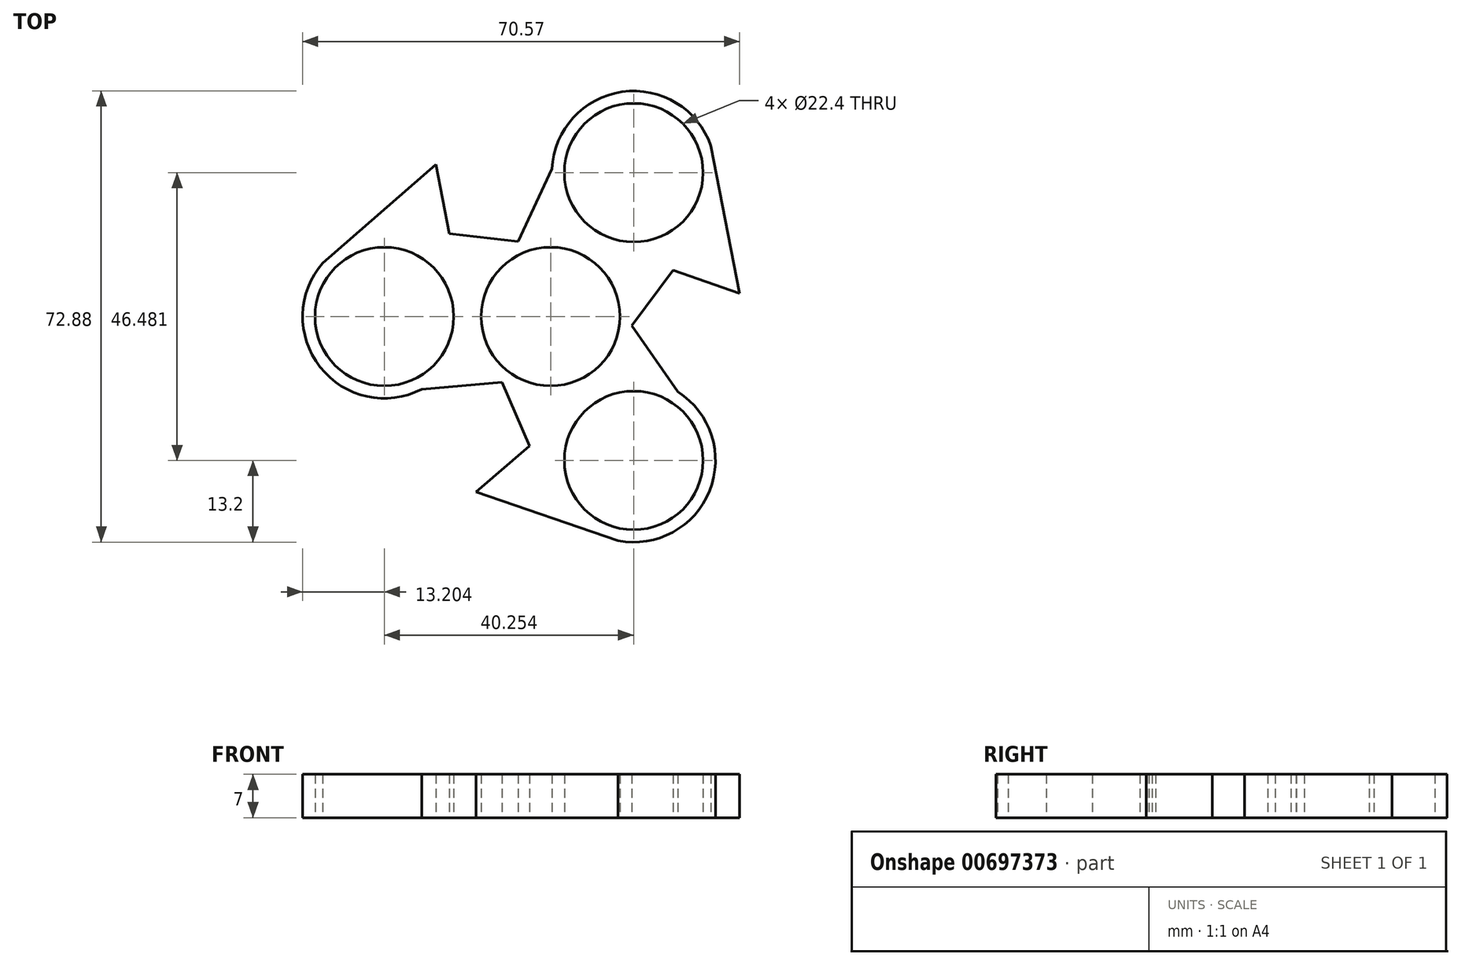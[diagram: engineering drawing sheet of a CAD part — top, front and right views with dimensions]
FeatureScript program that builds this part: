
annotation { "Feature Type Name" : "Feature", "Feature Type Description" : "" }
export const myFeature = defineFeature(function(context is Context, id is Id, definition is map)
    precondition{}
    {
        {
            var Q0;
            Q0=qCreatedBy(makeId("Top.planeOp"),FACE);
            var sketch = newSketch(context, id + "F0", { "sketchPlane" : qUnion([Q0])});
            skCircle(sketch, "E0", {"center": v(0, 0) * mm, "radius": 11.2 * mm});
            skCircle(sketch, "E1", {"center": v(-26.84, 0) * mm, "radius": 11.2 * mm});
            skArc(sketch, "E2", {"start": v(-34.03, 11.07) * mm, "mid": v(-38.25, -6.63) * mm, "end": v(-20.79, -11.73) * mm});
            skCircle(sketch, "E3.1.0", {"center": v(13.42, -23.24) * mm, "radius": 11.2 * mm});
            skArc(sketch, "E3.1.1", {"start": v(7.43, -35) * mm, "mid": v(24.87, -29.8) * mm, "end": v(20.55, -12.13) * mm});
            skCircle(sketch, "E3.2.0", {"center": v(13.42, 23.24) * mm, "radius": 11.2 * mm});
            skArc(sketch, "E3.2.1", {"start": v(26.6, 23.94) * mm, "mid": v(13.38, 36.44) * mm, "end": v(0.23, 23.87) * mm});
            skLineSegment(sketch, "E4", {"start": v(25.9, 27.54) * mm, "end": v(30.53, 3.73) * mm});
            skLineSegment(sketch, "E5", {"start": v(30.53, 3.73) * mm, "end": v(12.3, 10.09) * mm});
            skLineSegment(sketch, "E6.1.0", {"start": v(-18.5, 24.58) * mm, "end": v(-14.9, 5.62) * mm});
            skLineSegment(sketch, "E6.1.1", {"start": v(-36.8, 8.66) * mm, "end": v(-18.5, 24.58) * mm});
            skLineSegment(sketch, "E6.2.0", {"start": v(-12.04, -28.3) * mm, "end": v(2.58, -15.7) * mm});
            skLineSegment(sketch, "E6.2.1", {"start": v(10.9, -36.2) * mm, "end": v(-12.04, -28.3) * mm});
            skLineSegment(sketch, "E7", {"start": v(-20.79, -11.73) * mm, "end": v(-7.85, -10.61) * mm});
            skLineSegment(sketch, "E8", {"start": v(-7.85, -10.61) * mm, "end": v(-3.4, -20.87) * mm});
            skLineSegment(sketch, "E9.1.0", {"start": v(20.55, -12.13) * mm, "end": v(13.12, -1.5) * mm});
            skLineSegment(sketch, "E9.1.1", {"start": v(13.12, -1.5) * mm, "end": v(19.77, 7.48) * mm});
            skLineSegment(sketch, "E9.2.0", {"start": v(0.23, 23.87) * mm, "end": v(-5.26, 12.1) * mm});
            skLineSegment(sketch, "E9.2.1", {"start": v(-5.26, 12.1) * mm, "end": v(-16.37, 13.38) * mm});
            skSolve(sketch);
        }
        {
            var Q0;
            Q0=makeQuery(id+"F0.imprint","IMPRINT",FACE,{"disambiguationData":[TD([[makeQuery(id+"F0.imprint","IMPRINT",EDGE,{"derivedFrom":sQuery(id+"F0.wireOp",EDGE,"E0")}),-1.0]])]});
            extrude(context, id + "F1", {"entities" : qUnion([Q0]), "depth" : 7 * mm, "offsetDistance" : 25 * mm});
        }
    });
